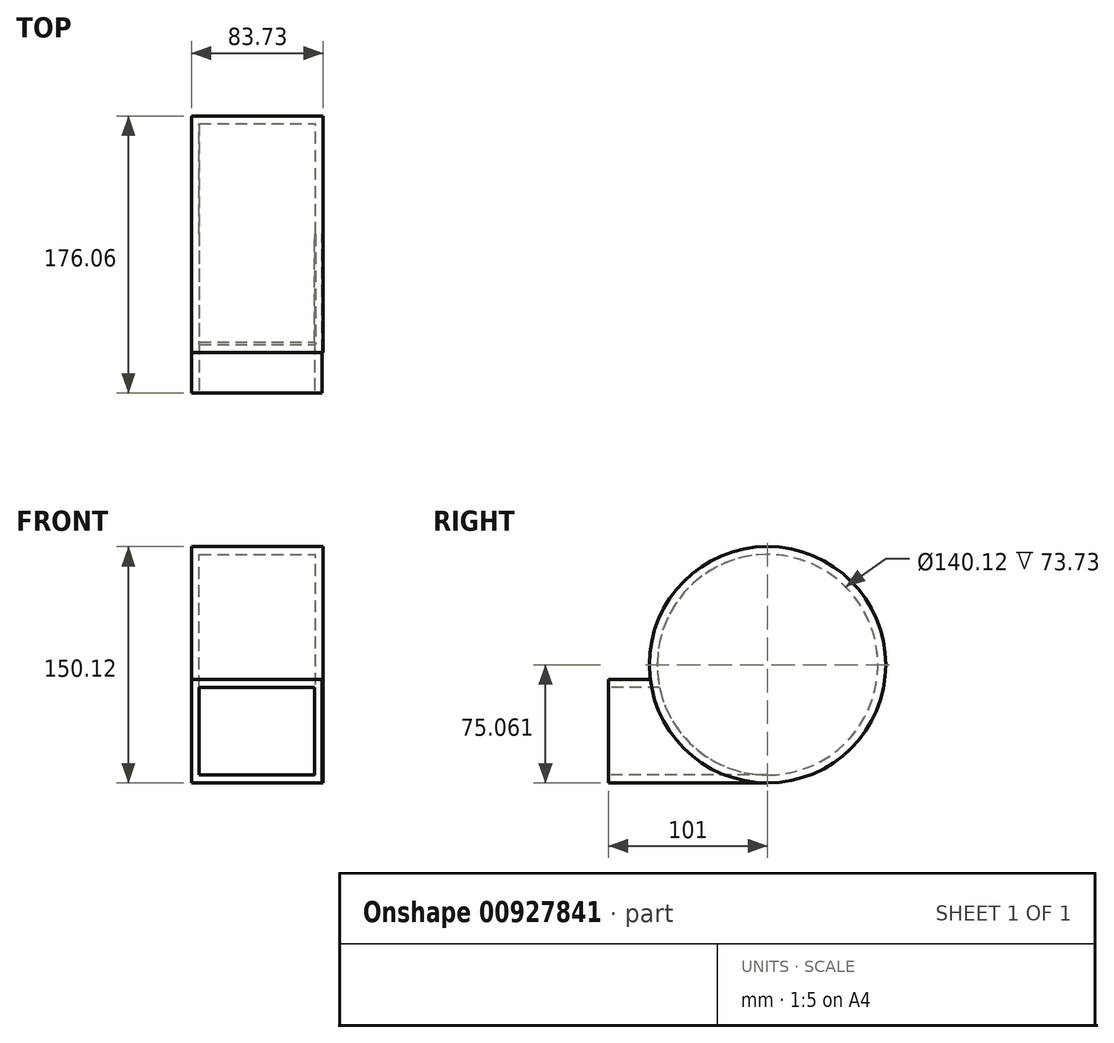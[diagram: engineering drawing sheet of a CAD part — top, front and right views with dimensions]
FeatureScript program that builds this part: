
annotation { "Feature Type Name" : "Feature", "Feature Type Description" : "" }
export const myFeature = defineFeature(function(context is Context, id is Id, definition is map)
    precondition{}
    {
        {
            var Q0;
            Q0=qCreatedBy(makeId("Front.planeOp"),FACE);
            var sketch = newSketch(context, id + "F0", { "sketchPlane" : qUnion([Q0])});
            skLineSegment(sketch, "E0", {"start": v(0, 0) * mm, "end": v(83.73, 0) * mm});
            skLineSegment(sketch, "E1", {"start": v(83.73, 0) * mm, "end": v(83.73, 75.06) * mm});
            skLineSegment(sketch, "E2", {"start": v(83.73, 75.06) * mm, "end": v(0, 75.06) * mm});
            skLineSegment(sketch, "E3", {"start": v(0, 75.06) * mm, "end": v(0, 0) * mm});
            skSolve(sketch);
        }
        {
            var Q0;
            Q0=qCreatedBy(makeId("Top.planeOp"),FACE);
            var sketch = newSketch(context, id + "F1", { "sketchPlane" : qUnion([Q0])});
            skLineSegment(sketch, "E4.bottom", {"start": v(0, 0) * mm, "end": v(83.07, 0) * mm});
            skLineSegment(sketch, "E4.top", {"start": v(0, -101) * mm, "end": v(83.07, -101) * mm});
            skLineSegment(sketch, "E4.left", {"start": v(0, 0) * mm, "end": v(0, -101) * mm});
            skLineSegment(sketch, "E4.right", {"start": v(83.07, 0) * mm, "end": v(83.07, -101) * mm});
            skSolve(sketch);
        }
        {
            var Q0;
            Q0=makeQuery(id+"F1.imprint","IMPRINT",FACE,{"disambiguationData":[TD([[makeQuery(id+"F1.imprint","IMPRINT",EDGE,{"derivedFrom":sQuery(id+"F1.wireOp",EDGE,"E4.bottom")}),-1.0]])]});
            var Q1;
            Q1 = qSketchRegion(id + "F1", true);
            extrude(context, id + "F2", {"entities" : qUnion([Q0, Q1]), "depth" : 65.7 * mm, "offsetDistance" : 25 * mm});
        }
        {
            var Q0;
            Q0=makeQuery(id+"F0.imprint","IMPRINT",FACE,{"disambiguationData":[TD([[makeQuery(id+"F0.imprint","IMPRINT",EDGE,{"derivedFrom":sQuery(id+"F0.wireOp",EDGE,"E0")}),1.0]])]});
            var Q1;
            Q1=sQuery(id+"F0.wireOp",EDGE,"E2");
            revolve(context, id + "F3", {"operationType" : NewBodyOperationType.ADD, "surfaceOperationType" : NewSurfaceOperationType.NEW, "entities" : qUnion([Q0]), "axis" : qUnion([Q1]), "revolveType" : RevolveType.FULL});
        }
        {
            var Q0;
            Q0=makeQuery(id+"F2.opExtrude","SWEPT_FACE",FACE,{"disambiguationData":[OSD([sQuery(id+"F1.wireOp",EDGE,"E4.top")])]});
            shell(context, id + "F4", {"entities" : qUnion([Q0]), "thickness" : 5 * mm});
        }
    });
